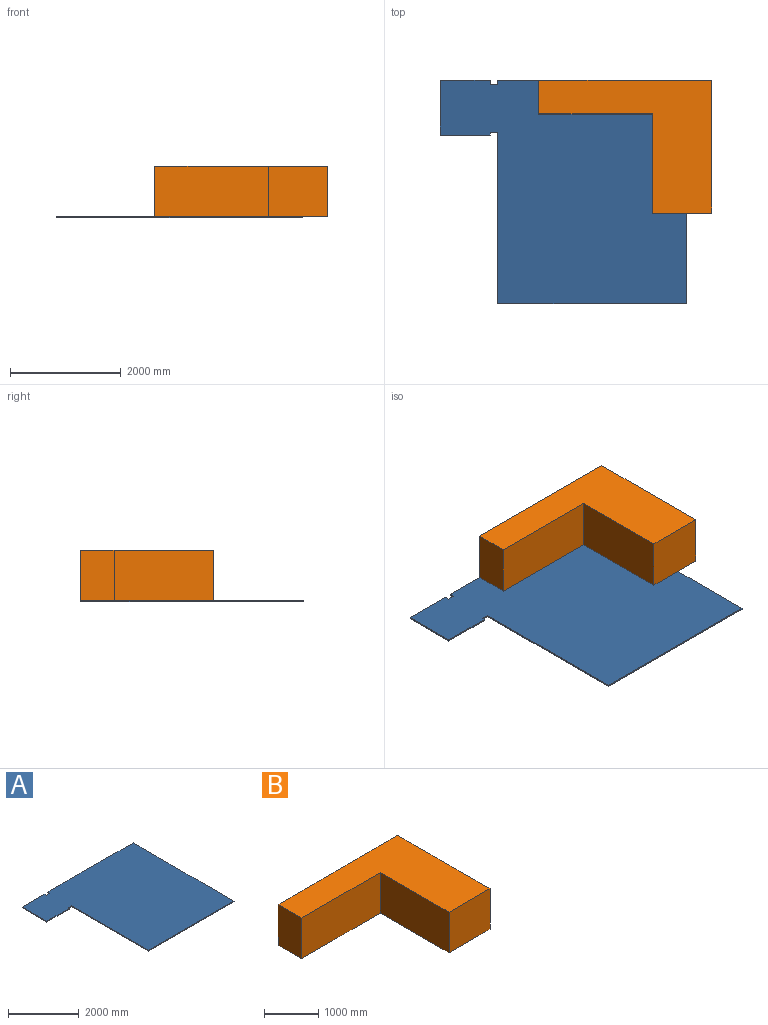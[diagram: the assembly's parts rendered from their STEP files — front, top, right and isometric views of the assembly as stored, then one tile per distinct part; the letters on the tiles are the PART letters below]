
ASSEMBLY  parts=2 mates=1
PART A: 16 faces, bbox 4447.7x4038.6x25.4 mm
  f0: plane 901.7x25.4mm, normal (0,1,0), area 22903.2mm2, adj f1,f13,f14,f15
  f1: plane 990.6x25.4mm, normal (-1,0,0), area 25161.2mm2, adj f0,f2,f14,f15
  f2: plane 904.4x25.4mm, normal (0,-1,0), area 22971.8mm2, adj f1,f3,f14,f15
  f3: plane 44.45x25.4mm, normal (1,0,0), area 1129mm2, adj f2,f4,f14,f15
  f4: plane 133.35x25.4mm, normal (0,-1,0), area 3387.1mm2, adj f3,f5,f14,f15
  f5: plane 3092.45x25.4mm, normal (-1,0,0), area 78548.2mm2, adj f4,f6,f14,f15
  f6: plane 3409.95x25.4mm, normal (0,-1,0), area 86612.7mm2, adj f5,f7,f14,f15
  f7: plane 831.85x25.4mm, normal (1,0,0), area 21129mm2, adj f6,f8,f14,f15
  f8: plane 806.45x25.4mm, normal (1,0,0), area 20483.9mm2, adj f7,f9,f14,f15
  f9: plane 2400.3x25.4mm, normal (1,0,0), area 60967.6mm2, adj f8,f10,f14,f15
  f10: plane 3413.13x25.4mm, normal (0,1,0), area 86693.4mm2, adj f9,f11,f14,f15
  f11: plane 82.55x25.4mm, normal (-1,0,0), area 2096.8mm2, adj f10,f12,f14,f15
  f12: plane 130.18x25.4mm, normal (0,1,0), area 3306.4mm2, adj f11,f13,f14,f15
  f13: plane 82.55x25.4mm, normal (1,0,0), area 2096.8mm2, adj f0,f12,f14,f15
  f14: plane 4447.7x4038.6mm, normal (0,0,-1), area 14775171.4mm2, adj f0,f1,f2,f3,f4,f5,f6,f7
  f15: plane 4447.7x4038.6mm, normal (0,0,1), area 14775171.4mm2, adj f0,f1,f2,f3,f4,f5,f6,f7
PART B: 8 faces, bbox 3124.2x2400.3x914.4 mm
  f0: plane 3124.2x914.4mm, normal (0,1,0), area 2856768.5mm2, adj f1,f5,f6,f7
  f1: plane 914.4x609.6mm, normal (-1,0,0), area 557418.2mm2, adj f0,f2,f6,f7
  f2: plane 2057.4x914.4mm, normal (0,-1,0), area 1881286.6mm2, adj f1,f3,f6,f7
  f3: plane 1790.7x914.4mm, normal (-1,0,0), area 1637416.1mm2, adj f2,f4,f6,f7
  f4: plane 1066.8x914.4mm, normal (0,-1,0), area 975481.9mm2, adj f3,f5,f6,f7
  f5: plane 2400.3x914.4mm, normal (1,0,0), area 2194834.3mm2, adj f0,f4,f6,f7
  f6: plane 3124.2x2400.3mm, normal (0,0,1), area 3814831.1mm2, adj f0,f1,f2,f3,f4,f5
  f7: plane 3124.2x2400.3mm, normal (0,0,-1), area 3814831.1mm2, adj f0,f1,f2,f3,f4,f5
PLACE A t=(5297.43,1459.99,1990.71)mm
PLACE B t=(6247.5,2881.54,1990.71)mm
MATE fastened B.f7 <-> A.f15  axis (0,0,1) through (7669.05,4046.58,1990.71)mm
